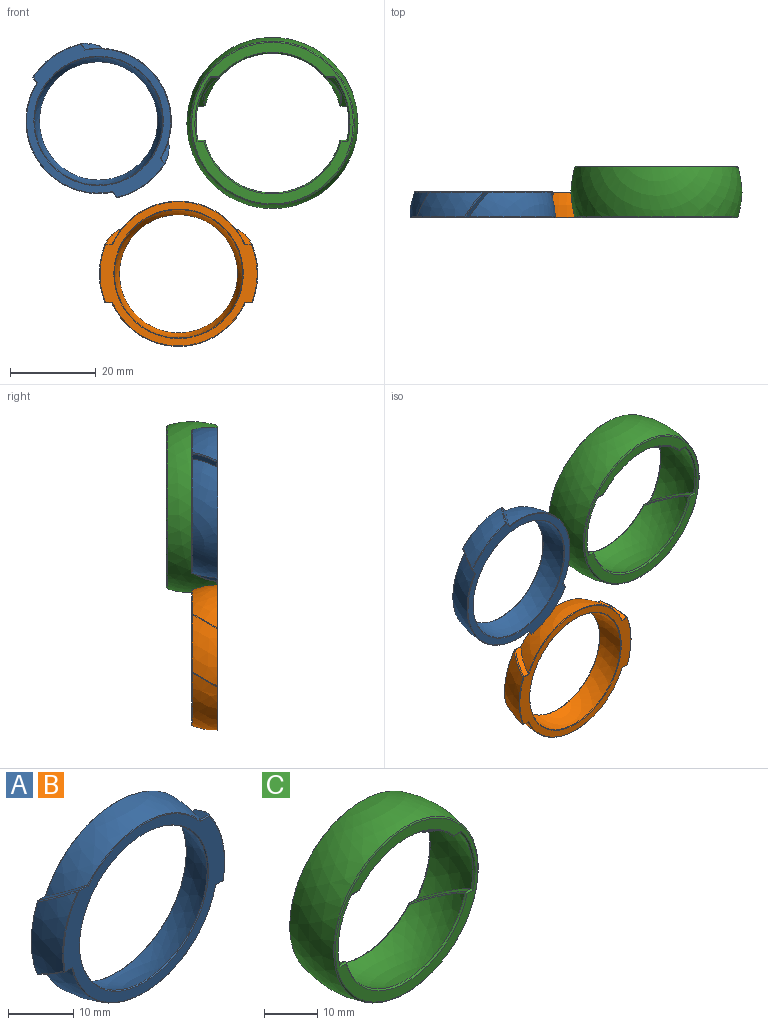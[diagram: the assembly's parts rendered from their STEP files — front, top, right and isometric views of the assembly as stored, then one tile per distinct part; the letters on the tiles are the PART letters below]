
ASSEMBLY  parts=3 mates=2
PART A: 33 faces, bbox 37x30x34 mm
  f0: sphere r=15mm, area 536.1mm2, adj f19,f28
  f1: plane 34.81x31.63mm, normal (0,-1,0), area 220.4mm2, adj f20,f21,f22,f23,f24,f25,f26,f27
  f2: sphere r=17mm, area 200.4mm2, adj f3,f4,f13,f21,f23,f25
  f3: plane 5.74x4.7mm, normal (0,0.5,0.87), area 10.3mm2, adj f2,f11,f13,f21,f32
  f4: plane 5.74x4.7mm, normal (0,0.5,0.87), area 10.3mm2, adj f2,f13,f15,f25,f29
  f5: sphere r=18.5mm, area 81.5mm2, adj f12,f20,f31,f32
  f6: sphere r=18.5mm, area 81.5mm2, adj f17,f27,f29,f30
  f7: plane 5.74x3.31mm, normal (0,-0.5,-0.87), area 9.3mm2, adj f9,f14,f22,f24,f31
  f8: plane 5.74x3.31mm, normal (0,-0.5,-0.87), area 9.3mm2, adj f9,f18,f24,f26,f30
  f9: sphere r=17mm, area 246.7mm2, adj f7,f8,f14,f16,f18,f24
  f10: plane 36.74x33.74mm, normal (0,1,0), area 216.5mm2, adj f11,f12,f13,f14,f15,f16,f17,f18
  f11: plane 1.63x0.11mm, normal (0,0.87,0.5), area 0.2mm2, adj f3,f10,f12,f13,f32
  f12: cone r=18.37mm half-angle=44.8deg, axis (0,-1,0), area 2.6mm2, adj f5,f10,f11,f14,f31,f32
  f13: cone r=17mm half-angle=44.8deg, axis (0,-1,0), area 7.2mm2, adj f2,f3,f4,f10,f11,f15
  f14: plane 1.68x0.2mm, normal (0,0.5,-0.87), area 0.4mm2, adj f7,f9,f10,f12,f16,f31
  f15: plane 1.63x0.11mm, normal (0,0.87,0.5), area 0.2mm2, adj f4,f10,f13,f17,f29
  f16: cone r=17mm half-angle=44.8deg, axis (0,-1,0), area 7.3mm2, adj f9,f10,f14,f18
  f17: cone r=18.37mm half-angle=44.8deg, axis (0,-1,0), area 2.6mm2, adj f6,f10,f15,f18,f29,f30
  f18: plane 1.68x0.2mm, normal (0,0.5,-0.87), area 0.4mm2, adj f8,f9,f10,f16,f17,f30
  f19: cone r=15.13mm half-angle=45.2deg, axis (0,1,0), area 17.5mm2, adj f0,f10
  f20: cone r=17.53mm half-angle=54.3deg, axis (0,1,0), area 2.2mm2, adj f1,f5,f21,f31,f32
  f21: plane 2.07x0.2mm, normal (0,-0.5,0.87), area 0.4mm2, adj f1,f2,f3,f20,f23,f32
  f22: plane 1.59x0.11mm, normal (0,-0.87,-0.5), area 0.2mm2, adj f1,f7,f24,f31
  f23: cone r=15.82mm half-angle=55.2deg, axis (0,1,0), area 4.1mm2, adj f1,f2,f21,f25
  f24: cone r=15.82mm half-angle=55.2deg, axis (0,1,0), area 6.4mm2, adj f1,f7,f8,f9,f22,f26
  f25: plane 2.07x0.2mm, normal (0,-0.5,0.87), area 0.4mm2, adj f1,f2,f4,f23,f27,f29
  f26: plane 1.59x0.11mm, normal (0,-0.87,-0.5), area 0.2mm2, adj f1,f8,f24,f30
  f27: cone r=17.53mm half-angle=54.3deg, axis (0,1,0), area 2.2mm2, adj f1,f6,f25,f29,f30
  f28: cone r=13.83mm half-angle=33.6deg, axis (0,-1,0), area 19mm2, adj f0,f1
  f29: cone r=17.56mm half-angle=54.1deg, axis (0,-0.5,-0.87), area 2.4mm2, adj f4,f6,f15,f17,f25,f27
  f30: cone r=17.3mm half-angle=54.1deg, axis (0,0.5,0.87), area 2.2mm2, adj f1,f6,f8,f17,f18,f26,f27
  f31: cone r=17.3mm half-angle=54.1deg, axis (0,0.5,0.87), area 2.2mm2, adj f1,f5,f7,f12,f14,f20,f22
  f32: cone r=17.56mm half-angle=54.1deg, axis (0,-0.5,-0.87), area 2.4mm2, adj f3,f5,f11,f12,f20,f21
PART B: same geometry as A
PART C: 33 faces, bbox 40x40x40 mm
  f0: sphere r=17.25mm, area 432.8mm2, adj f14,f23,f29,f31
  f1: plane 11.46x6.61mm, normal (0,-0.5,-0.87), area 19.7mm2, adj f3,f12,f20,f21,f23,f31
  f2: plane 11.46x6.61mm, normal (0,-0.5,-0.87), area 19.7mm2, adj f4,f16,f23,f25,f27,f29
  f3: sphere r=18.75mm, area 171.3mm2, adj f1,f5,f11,f12,f20,f22
  f4: sphere r=18.75mm, area 171.3mm2, adj f2,f6,f16,f18,f26,f27
  f5: plane 11.46x6.61mm, normal (0,0.5,0.87), area 19.7mm2, adj f3,f11,f13,f15,f22,f32
  f6: plane 11.46x6.61mm, normal (0,0.5,0.87), area 19.7mm2, adj f4,f15,f17,f18,f26,f30
  f7: sphere r=17.25mm, area 432.8mm2, adj f15,f24,f30,f32
  f8: plane 37.76x37.76mm, normal (0,1,0), area 207.5mm2, adj f11,f12,f13,f14,f15,f16,f17,f18
  f9: plane 37.76x37.76mm, normal (0,-1,0), area 207.5mm2, adj f20,f21,f22,f23,f24,f25,f26,f27
  f10: sphere r=20mm, area 1459.1mm2, adj f19,f28
  f11: cone r=17.88mm half-angle=36.2deg, axis (0,1,0), area 6.8mm2, adj f3,f5,f8,f12,f13
  f12: plane 1.8x0.41mm, normal (0,0.5,-0.87), area 0.8mm2, adj f1,f3,f8,f11,f14,f31
  f13: plane 2.08x0.24mm, normal (0,0.87,0.5), area 0.5mm2, adj f5,f8,f11,f15
  f14: cone r=16.56mm half-angle=35.5deg, axis (0,1,0), area 19.2mm2, adj f0,f8,f12,f16,f29,f31
  f15: cone r=16.56mm half-angle=35.5deg, axis (0,1,0), area 12.6mm2, adj f5,f6,f7,f8,f13,f17,f30,f32
  f16: plane 1.8x0.41mm, normal (0,0.5,-0.87), area 0.8mm2, adj f2,f4,f8,f14,f18,f29
  f17: plane 2.08x0.24mm, normal (0,0.87,0.5), area 0.5mm2, adj f6,f8,f15,f18
  f18: cone r=17.88mm half-angle=36.2deg, axis (0,1,0), area 6.8mm2, adj f4,f6,f8,f16,f17
  f19: cone r=19.14mm half-angle=53.4deg, axis (0,-1,0), area 38.8mm2, adj f8,f10
  f20: cone r=18.14mm half-angle=36.2deg, axis (0,-1,0), area 6.8mm2, adj f1,f3,f9,f21,f22
  f21: plane 2.08x0.24mm, normal (0,-0.87,-0.5), area 0.5mm2, adj f1,f9,f20,f23
  f22: plane 1.8x0.41mm, normal (0,-0.5,0.87), area 0.8mm2, adj f3,f5,f9,f20,f24,f32
  f23: cone r=16.3mm half-angle=35.5deg, axis (0,-1,0), area 12.6mm2, adj f0,f1,f2,f9,f21,f25,f29,f31
  f24: cone r=16.3mm half-angle=35.5deg, axis (0,-1,0), area 19.2mm2, adj f7,f9,f22,f26,f30,f32
  f25: plane 2.08x0.24mm, normal (0,-0.87,-0.5), area 0.5mm2, adj f2,f9,f23,f27
  f26: plane 1.8x0.41mm, normal (0,-0.5,0.87), area 0.8mm2, adj f4,f6,f9,f24,f27,f30
  f27: cone r=18.14mm half-angle=36.2deg, axis (0,-1,0), area 6.8mm2, adj f2,f4,f9,f25,f26
  f28: cone r=18.88mm half-angle=53.4deg, axis (0,1,0), area 38.8mm2, adj f9,f10
  f29: cone r=16.01mm half-angle=55.9deg, axis (0,-0.5,-0.87), area 4.6mm2, adj f0,f2,f14,f16,f23
  f30: cone r=16.01mm half-angle=55.9deg, axis (0,0.5,0.87), area 4.6mm2, adj f6,f7,f15,f24,f26
  f31: cone r=16.01mm half-angle=55.9deg, axis (0,-0.5,-0.87), area 4.6mm2, adj f0,f1,f12,f14,f23
  f32: cone r=16.01mm half-angle=55.9deg, axis (0,0.5,0.87), area 4.6mm2, adj f5,f7,f15,f22,f24
PLACE A rot(axis=(-0.46,0,-0.89),180deg) t=(-36.37,-0.98,4.34)mm
PLACE B rot(axis=(0,0,1),180deg) t=(-17.68,-0.98,-31.39)mm
PLACE C t=(4.26,5.02,3.84)mm fixed
MATE planar B.f10 <-> C.f9  axis (0,-1,0) through (-33.1,-0.98,-24.54)mm
MATE planar A.f10 <-> B.f10  axis (0,-1,0) through (-36.36,-0.98,4.35)mm
